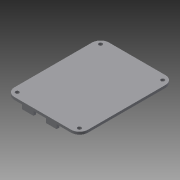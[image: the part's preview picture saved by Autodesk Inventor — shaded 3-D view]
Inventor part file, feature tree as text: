
AUTODESK INVENTOR PART (.ipt)
format: ipt  version: 2014 (Build 180170000, 170)  size: 141,824 bytes
history: native  units: mm
features: reference x5, extrude x3, sketch x3
ambient origin geometry x8: Origin, YZ Plane, XZ Plane, XY Plane, X Axis, Y Axis, Z Axis, Center Point
bodies: Solid1 (feature_tree)
feature tree (11):
  extrude  "Extrusion1"  Depth=2.4mm
  extrude  "Extrusion2"  Depth=10.0mm
  extrude  "Extrusion3"  Depth=4.0mm
  sketch  "Sketch1"  dims[d0=2.4mm d1=0.0mm d2=50.0mm]
  reference  "Reference1"
  sketch  "Sketch2"  dims[d3=60.0mm d4=10.0mm]
  sketch  "Sketch3"  dims[d5=2.5mm d6=6.0mm d7=2.5mm d8=6.0mm d9=2.5mm d10=6.0mm d11=2.5mm d12=6.0mm d13=4.0mm d14=0.0mm d15=4.0mm d16=0.0mm]
  reference  "Reference2"
  reference  "Reference3"
  reference  "Reference4"
  reference  "Reference5"
